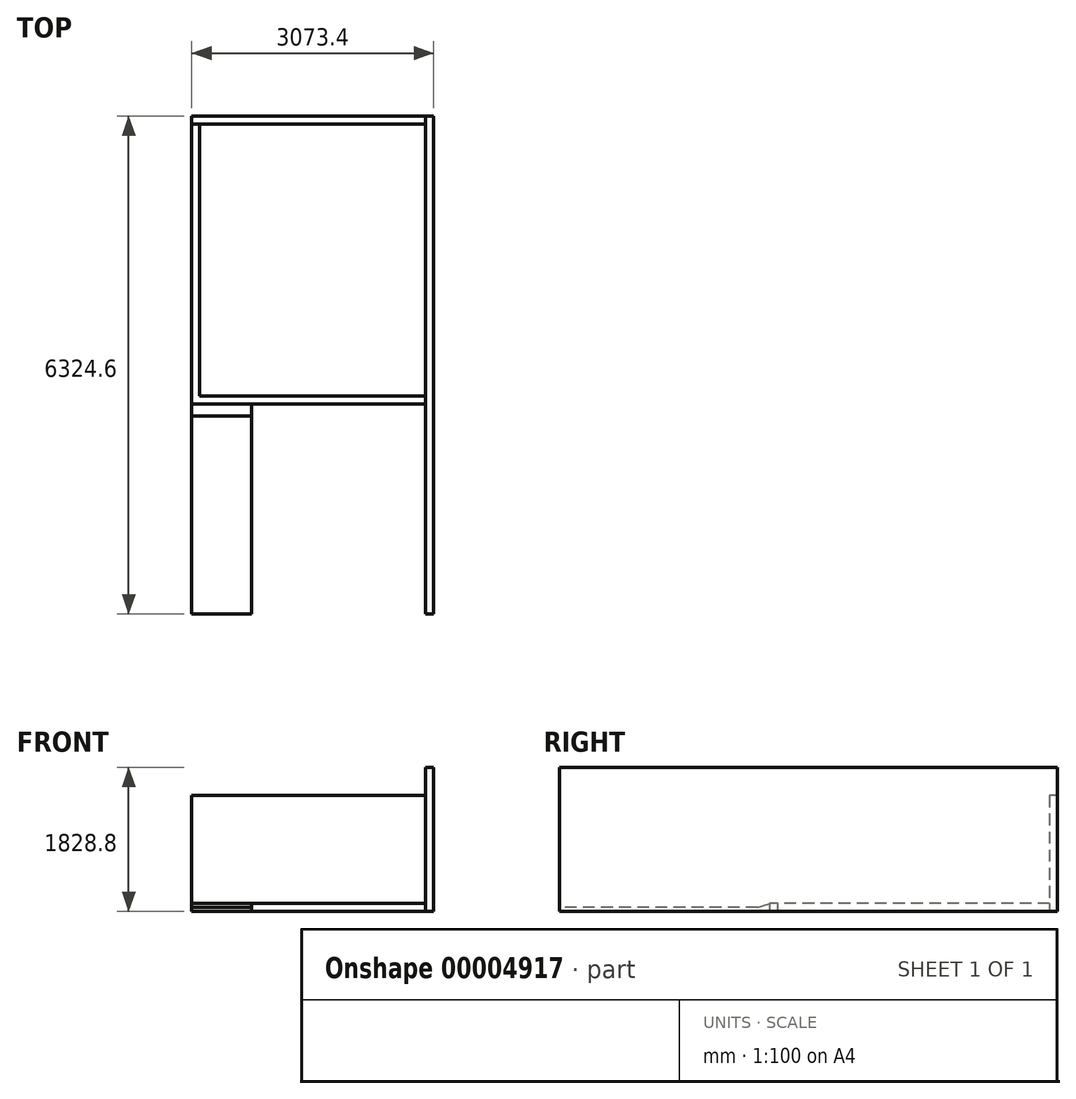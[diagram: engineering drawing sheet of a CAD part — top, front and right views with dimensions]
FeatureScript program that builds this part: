
annotation { "Feature Type Name" : "Feature", "Feature Type Description" : "" }
export const myFeature = defineFeature(function(context is Context, id is Id, definition is map)
    precondition{}
    {
        {
            var Q0;
            Q0=qCreatedBy(makeId("Top.planeOp"),FACE);
            var sketch = newSketch(context, id + "F0", { "sketchPlane" : qUnion([Q0])});
            skLineSegment(sketch, "E0.bottom", {"start": v(0, 0) * mm, "end": v(-2971.8, 0) * mm});
            skLineSegment(sketch, "E0.top", {"start": v(0, -6223) * mm, "end": v(-2971.8, -6223) * mm});
            skLineSegment(sketch, "E0.left", {"start": v(0, 0) * mm, "end": v(0, -6223) * mm});
            skLineSegment(sketch, "E0.right", {"start": v(-2971.8, 0) * mm, "end": v(-2971.8, -6223) * mm});
            skLineSegment(sketch, "E1", {"start": v(0, -3556) * mm, "end": v(-2971.8, -3556) * mm});
            skLineSegment(sketch, "E2", {"start": v(-2870.2, 0) * mm, "end": v(-2870.2, -3454.4) * mm});
            skLineSegment(sketch, "E3", {"start": v(-2870.2, -3454.4) * mm, "end": v(0, -3454.4) * mm});
            skLineSegment(sketch, "E4", {"start": v(-2209.8, -3556) * mm, "end": v(-2209.8, -6223) * mm});
            skLineSegment(sketch, "E5", {"start": v(-2209.8, -3708.4) * mm, "end": v(-2971.8, -3708.4) * mm});
            skSolve(sketch);
        }
        {
            var Q0;
            {var subQ1=sQuery(id+"F0.wireOp",EDGE,"E2");Q0=makeQuery(id+"F0.imprint","IMPRINT",FACE,{"disambiguationData":[TD([[makeQuery(id+"F0.imprint","IMPRINT",EDGE,{"derivedFrom":subQ1}),-1.0]])]});}
            extrude(context, id + "F1", {"entities" : qUnion([Q0]), "depth" : 101.6 * mm});
        }
        {
            var Q0;
            {var subQ1=sQuery(id+"F0.wireOp",EDGE,"E5");Q0=makeQuery(id+"F0.imprint","IMPRINT",FACE,{"disambiguationData":[TD([[makeQuery(id+"F0.imprint","IMPRINT",EDGE,{"derivedFrom":subQ1}),1.0]])]});}
            extrude(context, id + "F2", {"entities" : qUnion([Q0]), "depth" : 50.8 * mm});
        }
        {
            var Q0;
            Q0=makeQuery(id+"F1.opExtrude","SWEPT_FACE",FACE,{"disambiguationData":[OSD([sQuery(id+"F0.wireOp",EDGE,"E0.right")])]});
            var sketch = newSketch(context, id + "F3", { "sketchPlane" : qUnion([Q0])});
            skLineSegment(sketch, "E6", {"start": v(3556, 101.6) * mm, "end": v(3556, 0) * mm});
            skLineSegment(sketch, "E7", {"start": v(3556, 0) * mm, "end": v(3708.4, 0) * mm});
            skLineSegment(sketch, "E8", {"start": v(3708.4, 0) * mm, "end": v(3708.4, 50.8) * mm});
            skLineSegment(sketch, "E9", {"start": v(3708.4, 50.8) * mm, "end": v(3556, 101.6) * mm});
            skSolve(sketch);
        }
        {
            var Q0;
            Q0=makeQuery(id+"F3.imprint","IMPRINT",FACE,{"disambiguationData":[TD([[makeQuery(id+"F3.imprint","IMPRINT",EDGE,{"derivedFrom":sQuery(id+"F3.wireOp",EDGE,"E6")}),1.0]])]});
            var Q1;
            Q1=makeQuery(id+"F2.opExtrude","SWEPT_FACE",FACE,{"disambiguationData":[OSD([sQuery(id+"F0.wireOp",EDGE,"E4")])]});
            extrude(context, id + "F4", {"entities" : qUnion([Q0]), "operationType" : NewBodyOperationType.ADD, "endBound" : BoundingType.UP_TO_SURFACE, "oppositeDirection" : true, "endBoundEntityFace" : qUnion([Q1]), "depth" : 759.47 * mm});
        }
        {
            var Q0;
            Q0=qCreatedBy(makeId("Top.planeOp"),FACE);
            var sketch = newSketch(context, id + "F5", { "sketchPlane" : qUnion([Q0])});
            skLineSegment(sketch, "E10.0", {"start": v(0, 0) * mm, "end": v(-2971.8, 0) * mm});
            skLineSegment(sketch, "E11.0", {"start": v(0, 0) * mm, "end": v(0, -6223) * mm});
            skLineSegment(sketch, "E12", {"start": v(-2971.8, 0) * mm, "end": v(-2971.8, 101.6) * mm});
            skLineSegment(sketch, "E13", {"start": v(-2971.8, 101.6) * mm, "end": v(101.6, 101.6) * mm});
            skLineSegment(sketch, "E14", {"start": v(101.6, 101.6) * mm, "end": v(101.6, -6223) * mm});
            skLineSegment(sketch, "E15", {"start": v(101.6, -6223) * mm, "end": v(0, -6223) * mm});
            skSolve(sketch);
        }
        {
            var Q0;
            Q0=makeQuery(id+"F5.imprint","IMPRINT",FACE,{"disambiguationData":[TD([[makeQuery(id+"F5.imprint","IMPRINT",EDGE,{"derivedFrom":sQuery(id+"F5.wireOp",EDGE,"E10.0")}),-1.0]])]});
            extrude(context, id + "F6", {"entities" : qUnion([Q0]), "depth" : 1828.8 * mm});
        }
        {
            var Q0;
            Q0=makeQuery(id+"F6.opExtrude","SWEPT_FACE",FACE,{"disambiguationData":[OSD([sQuery(id+"F5.wireOp",EDGE,"E10.0")])]});
            var sketch = newSketch(context, id + "F7", { "sketchPlane" : qUnion([Q0])});
            skLineSegment(sketch, "E16.bottom", {"start": v(-2971.8, 1828.8) * mm, "end": v(0, 1828.8) * mm});
            skLineSegment(sketch, "E16.top", {"start": v(-2971.8, 1473.2) * mm, "end": v(0, 1473.2) * mm});
            skLineSegment(sketch, "E16.left", {"start": v(-2971.8, 1828.8) * mm, "end": v(-2971.8, 1473.2) * mm});
            skLineSegment(sketch, "E16.right", {"start": v(0, 1828.8) * mm, "end": v(0, 1473.2) * mm});
            skSolve(sketch);
        }
        {
            var Q0;
            Q0=makeQuery(id+"F7.imprint","IMPRINT",FACE,{"disambiguationData":[TD([[makeQuery(id+"F7.imprint","IMPRINT",EDGE,{"derivedFrom":sQuery(id+"F7.wireOp",EDGE,"E16.bottom")}),1.0]])]});
            extrude(context, id + "F8", {"entities" : qUnion([Q0]), "operationType" : NewBodyOperationType.REMOVE, "endBound" : BoundingType.THROUGH_ALL, "oppositeDirection" : true, "depth" : 25.4 * mm});
        }
    });
